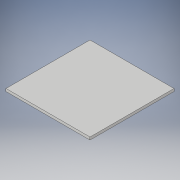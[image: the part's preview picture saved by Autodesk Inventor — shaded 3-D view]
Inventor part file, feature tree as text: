
AUTODESK INVENTOR PART (.ipt)
format: ipt  version: 2019 (Build 230136000, 136)  size: 89,088 bytes
history: native  units: in
note: dims shown in document units (in); Inventor stores cm internally (conversion verified against a paired STEP export)
features: extrude x1, sketch x1
ambient origin geometry x8: Origin, YZ Plane, XZ Plane, XY Plane, X Axis, Y Axis, Z Axis, Center Point
bodies: Solid1 (feature_tree)
feature tree (2):
  extrude  "Extrusion1"  Depth=4.0in
  sketch  "Sketch1"  dims[d0=4.0in d1=4.0in d2=0.125in d3=0.0in]
